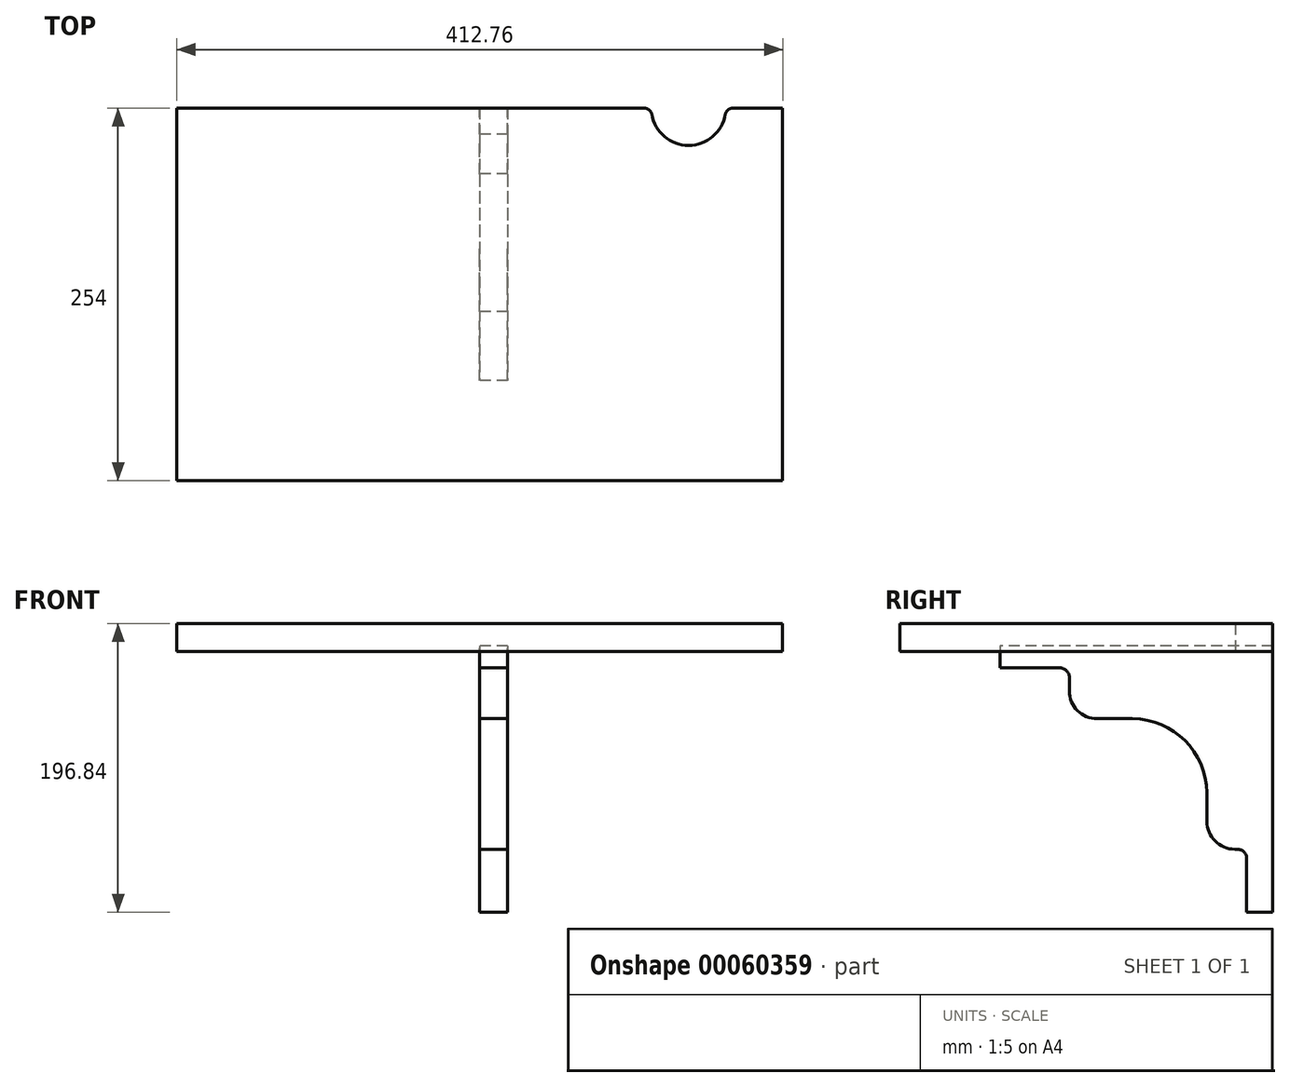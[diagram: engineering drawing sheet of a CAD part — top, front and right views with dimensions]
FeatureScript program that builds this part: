
annotation { "Feature Type Name" : "Feature", "Feature Type Description" : "" }
export const myFeature = defineFeature(function(context is Context, id is Id, definition is map)
    precondition{}
    {
        {
            var Q0;
            Q0=qCreatedBy(makeId("Front.planeOp"),FACE);
            var sketch = newSketch(context, id + "F0", { "sketchPlane" : qUnion([Q0])});
            skLineSegment(sketch, "E0.rect.bottom", {"start": v(206.38, -9.52) * mm, "end": v(-206.38, -9.53) * mm});
            skLineSegment(sketch, "E0.rect.top", {"start": v(206.38, 9.53) * mm, "end": v(-206.38, 9.52) * mm});
            skLineSegment(sketch, "E0.rect.left", {"start": v(206.38, -9.52) * mm, "end": v(206.38, 9.53) * mm});
            skLineSegment(sketch, "E0.rect.right", {"start": v(-206.38, -9.53) * mm, "end": v(-206.38, 9.52) * mm});
            skPoint(sketch, "E0.rect.middle", {"position": v(0, 0) * mm});
            skSolve(sketch);
        }
        {
            var Q0;
            Q0=makeQuery(id+"F0.imprint","IMPRINT",FACE,{"disambiguationData":[TD([[makeQuery(id+"F0.imprint","IMPRINT",EDGE,{"derivedFrom":sQuery(id+"F0.wireOp",EDGE,"E0.rect.bottom")}),-1.0]])]});
            extrude(context, id + "F1", {"entities" : qUnion([Q0]), "depth" : 254 * mm});
        }
        {
            var Q0;
            Q0=qCreatedBy(makeId("Right.planeOp"),FACE);
            var sketch = newSketch(context, id + "F2", { "sketchPlane" : qUnion([Q0])});
            skLineSegment(sketch, "E1", {"start": v(0, -5.8) * mm, "end": v(-185.79, -5.8) * mm});
            skLineSegment(sketch, "E2", {"start": v(-185.79, -5.8) * mm, "end": v(-185.79, -20.7) * mm});
            skLineSegment(sketch, "E3", {"start": v(-185.79, -20.7) * mm, "end": v(-145.03, -20.7) * mm});
            skLineSegment(sketch, "E4", {"start": v(-138.68, -27.05) * mm, "end": v(-138.68, -36.28) * mm});
            skLineSegment(sketch, "E5", {"start": v(-119.63, -55.33) * mm, "end": v(-103.3, -55.33) * mm});
            skLineSegment(sketch, "E6", {"start": v(-103.3, -55.33) * mm, "end": v(-95.62, -55.36) * mm});
            skLineSegment(sketch, "E7", {"start": v(-44.97, -105.79) * mm, "end": v(-44.92, -113.57) * mm});
            skLineSegment(sketch, "E8", {"start": v(-44.92, -113.57) * mm, "end": v(-44.92, -125.3) * mm});
            skLineSegment(sketch, "E9", {"start": v(-25.87, -144.35) * mm, "end": v(-24.14, -144.35) * mm});
            skLineSegment(sketch, "E10", {"start": v(-17.79, -150.7) * mm, "end": v(-17.79, -187.31) * mm});
            skLineSegment(sketch, "E11", {"start": v(-17.79, -187.31) * mm, "end": v(0, -187.31) * mm});
            skLineSegment(sketch, "E12", {"start": v(0, -187.31) * mm, "end": v(0, -5.8) * mm});
            skPoint(sketch, "E13.visualSharp", {"position": v(-45.34, -55.5) * mm});
            skArc(sketch, "E13.filletArc", {"start": v(-44.97, -105.79) * mm, "mid": v(-59.93, -70.16) * mm, "end": v(-95.62, -55.36) * mm});
            skPoint(sketch, "E14.visualSharp", {"position": v(-138.68, -55.33) * mm});
            skArc(sketch, "E14.filletArc", {"start": v(-138.68, -36.28) * mm, "mid": v(-133.1, -49.75) * mm, "end": v(-119.63, -55.33) * mm});
            skPoint(sketch, "E15.visualSharp", {"position": v(-44.92, -144.35) * mm});
            skArc(sketch, "E15.filletArc", {"start": v(-44.92, -125.3) * mm, "mid": v(-39.34, -138.77) * mm, "end": v(-25.87, -144.35) * mm});
            skPoint(sketch, "E16.visualSharp", {"position": v(-138.68, -20.7) * mm});
            skArc(sketch, "E16.filletArc", {"start": v(-138.68, -27.05) * mm, "mid": v(-140.53, -22.56) * mm, "end": v(-145.03, -20.7) * mm});
            skPoint(sketch, "E17.visualSharp", {"position": v(-17.79, -144.35) * mm});
            skArc(sketch, "E17.filletArc", {"start": v(-17.79, -150.7) * mm, "mid": v(-19.65, -146.2) * mm, "end": v(-24.14, -144.35) * mm});
            skSolve(sketch);
        }
        {
            var Q0;
            Q0=makeQuery(id+"F2.imprint","IMPRINT",FACE,{"disambiguationData":[TD([[makeQuery(id+"F2.imprint","IMPRINT",EDGE,{"derivedFrom":sQuery(id+"F2.wireOp",EDGE,"E1")}),1.0]])]});
            extrude(context, id + "F3", {"entities" : qUnion([Q0]), "depth" : 19.05 * mm});
        }
        {
            var Q0;
            Q0=qCreatedBy(makeId("Top.planeOp"),FACE);
            var sketch = newSketch(context, id + "F4", { "sketchPlane" : qUnion([Q0])});
            skCircle(sketch, "E18", {"center": v(142.22, 0) * mm, "radius": 25.4 * mm});
            skSolve(sketch);
        }
        {
            var Q0;
            Q0=makeQuery(id+"F4.imprint","IMPRINT",FACE,{"disambiguationData":[TD([[makeQuery(id+"F4.imprint","IMPRINT",EDGE,{"derivedFrom":sQuery(id+"F4.wireOp",EDGE,"E18")}),1.0]])]});
            var Q1;
            Q1=sQuery(id+"F4.wireOp",EDGE,"E18");
            extrude(context, id + "F5", {"entities" : qUnion([Q0]), "operationType" : NewBodyOperationType.REMOVE, "surfaceEntities" : qUnion([Q1]), "endBound" : BoundingType.SYMMETRIC, "depth" : 55.75 * mm});
        }
        {
            var Q0;
            Q0=makeQuery(id+"F5.boolean.opBoolean","INTERSECT",EDGE,{"disambiguationData":[OD(0.0)],"derivedFrom":[makeQuery(id+"F1.opExtrude","CAP_FACE",FACE,{"disambiguationData":[OSD([sQuery(id+"F0.wireOp",EDGE,"E0.rect.bottom"),sQuery(id+"F0.wireOp",EDGE,"E0.rect.top"),sQuery(id+"F0.wireOp",EDGE,"E0.rect.left"),sQuery(id+"F0.wireOp",EDGE,"E0.rect.right")])],"isStart":true}),makeQuery(id+"F5.opExtrude","SWEPT_FACE",FACE,{"disambiguationData":[OSD([sQuery(id+"F4.wireOp",EDGE,"E18")])]})]});
            var Q1;
            Q1=makeQuery(id+"F5.boolean.opBoolean","INTERSECT",EDGE,{"disambiguationData":[OD(1.0)],"derivedFrom":[makeQuery(id+"F1.opExtrude","CAP_FACE",FACE,{"disambiguationData":[OSD([sQuery(id+"F0.wireOp",EDGE,"E0.rect.bottom"),sQuery(id+"F0.wireOp",EDGE,"E0.rect.top"),sQuery(id+"F0.wireOp",EDGE,"E0.rect.left"),sQuery(id+"F0.wireOp",EDGE,"E0.rect.right")])],"isStart":true}),makeQuery(id+"F5.opExtrude","SWEPT_FACE",FACE,{"disambiguationData":[OSD([sQuery(id+"F4.wireOp",EDGE,"E18")])]})]});
            fillet(context, id + "F6", {"entities" : qUnion([Q0, Q1]), "radius" : 5.08 * mm, "tangentPropagation" : true, "allowEdgeOverflow" : false});
        }
    });
